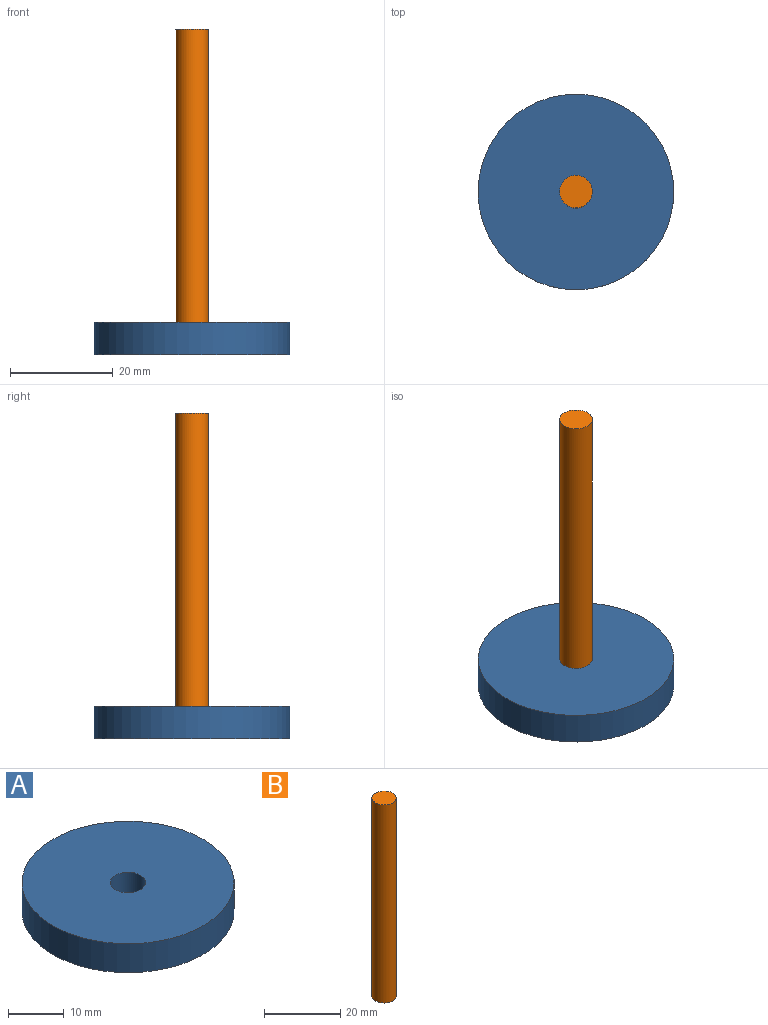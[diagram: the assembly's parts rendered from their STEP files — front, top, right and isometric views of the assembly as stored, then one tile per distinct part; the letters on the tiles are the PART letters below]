
ASSEMBLY  parts=2 mates=1
PART A: 4 faces, bbox 38.1x38.1x6.4 mm
  f0: cylinder r=3.17mm len=6.35mm, axis (0,0,-1), area 126.7mm2, adj f2,f3
  f1: cylinder r=19.05mm len=38.1mm, axis (0,0,-1), area 760.1mm2, adj f2,f3
  f2: plane 38.1x38.1mm, normal (0,0,1), area 1108.4mm2, adj f0,f1
  f3: plane 38.1x38.1mm, normal (0,0,-1), area 1108.4mm2, adj f0,f1
PART B: 3 faces, bbox 6.4x6.4x63.5 mm
  f0: plane 6.35x6.35mm, normal (0,0,1), area 31.7mm2, adj f1
  f1: cylinder r=3.17mm len=63.5mm, axis (0,0,-1), area 1266.8mm2, adj f0,f2
  f2: plane 6.35x6.35mm, normal (0,0,-1), area 31.7mm2, adj f1
PLACE A rot(axis=(0,0,1),0deg) t=(69.85,0,-69.85)mm
PLACE B rot(axis=(0,0,1),0deg) t=(69.85,0,-69.85)mm
MATE fastened B.f1 <-> A.f0  axis (0,0,-1) through (0,0,0)mm
